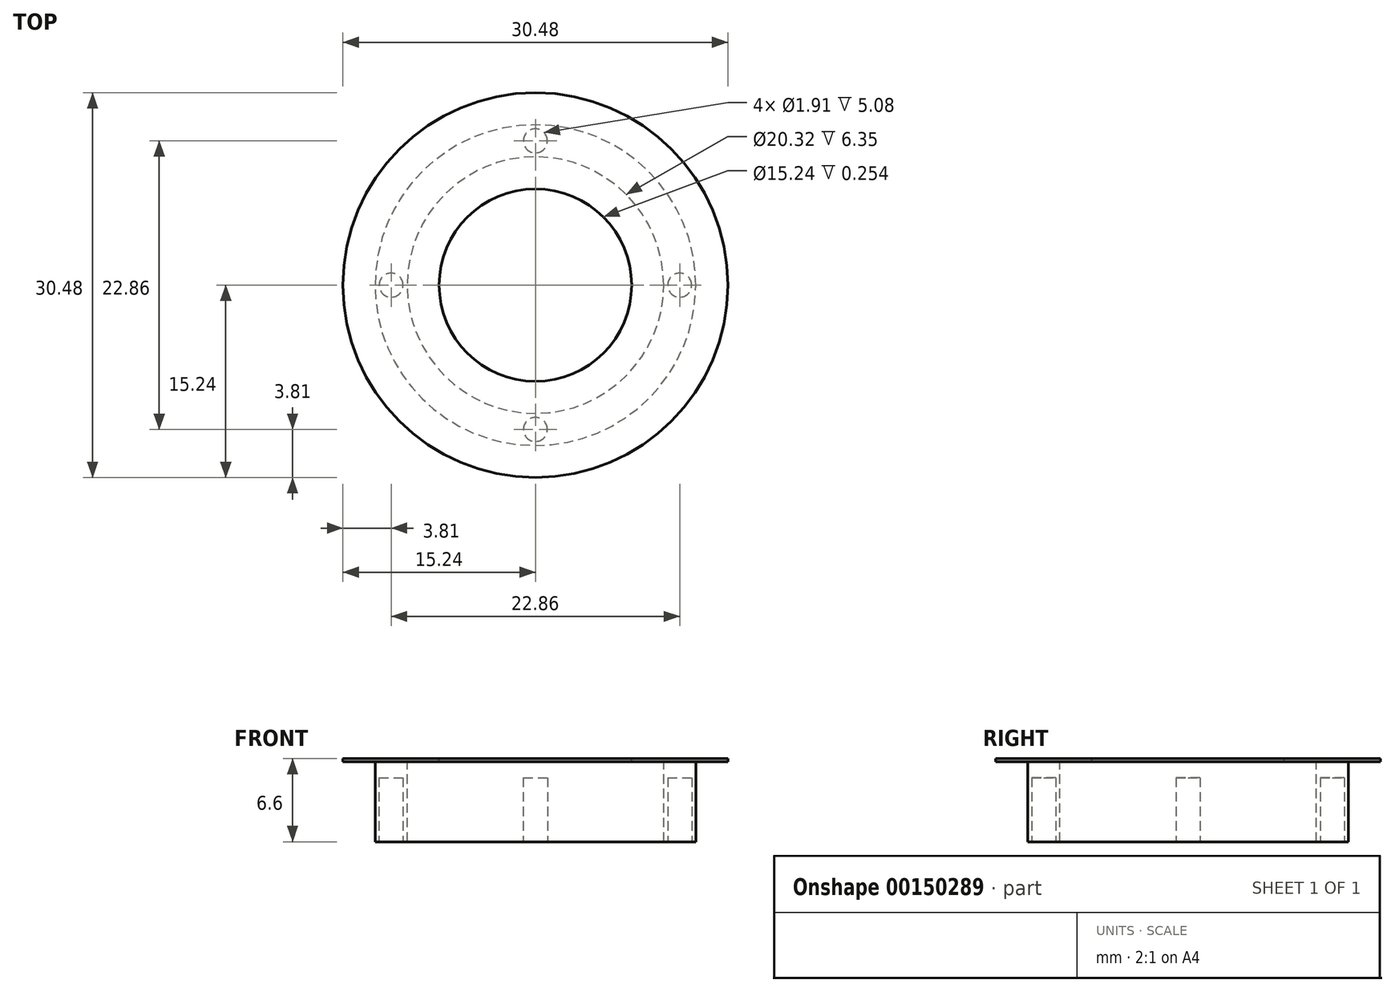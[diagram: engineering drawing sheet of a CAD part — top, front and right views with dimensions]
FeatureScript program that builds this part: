
annotation { "Feature Type Name" : "Feature", "Feature Type Description" : "" }
export const myFeature = defineFeature(function(context is Context, id is Id, definition is map)
    precondition{}
    {
        {
            var Q0;
            Q0=qCreatedBy(makeId("Front.planeOp"),FACE);
            var sketch = newSketch(context, id + "F0", { "sketchPlane" : qUnion([Q0])});
            skLineSegment(sketch, "E0.bottom", {"start": v(-12.7, 2.54) * mm, "end": v(-10.16, 2.54) * mm});
            skLineSegment(sketch, "E0.top", {"start": v(-12.7, -3.8) * mm, "end": v(-10.16, -3.8) * mm});
            skLineSegment(sketch, "E0.left", {"start": v(-12.7, 2.54) * mm, "end": v(-12.7, -3.8) * mm});
            skLineSegment(sketch, "E0.right", {"start": v(-10.16, 2.54) * mm, "end": v(-10.16, -3.8) * mm});
            skLineSegment(sketch, "E1.bottom", {"start": v(-12.7, 2.54) * mm, "end": v(-7.62, 2.54) * mm});
            skLineSegment(sketch, "E1.top", {"start": v(-12.7, 2.8) * mm, "end": v(-7.62, 2.8) * mm});
            skLineSegment(sketch, "E1.left", {"start": v(-12.7, 2.54) * mm, "end": v(-12.7, 2.8) * mm});
            skLineSegment(sketch, "E1.right", {"start": v(-7.62, 2.54) * mm, "end": v(-7.62, 2.8) * mm});
            skLineSegment(sketch, "E2", {"start": v(0, 2.9) * mm, "end": v(0, -2.8) * mm});
            skLineSegment(sketch, "E3.bottom", {"start": v(-12.7, 2.54) * mm, "end": v(-15.24, 2.54) * mm});
            skLineSegment(sketch, "E3.top", {"start": v(-12.7, 2.8) * mm, "end": v(-15.24, 2.8) * mm});
            skLineSegment(sketch, "E3.right", {"start": v(-15.24, 2.54) * mm, "end": v(-15.24, 2.8) * mm});
            skSolve(sketch);
        }
        {
            var Q0;
            Q0 = qSketchRegion(id + "F0", true);
            var Q1;
            Q1=sQuery(id+"F0.wireOp",EDGE,"E2");
            revolve(context, id + "F1", {"entities" : qUnion([Q0]), "axis" : qUnion([Q1]), "revolveType" : RevolveType.FULL});
        }
        {
            var Q0;
            Q0=makeQuery(id+"F1.opRevolve","SWEPT_FACE",FACE,{"disambiguationData":[OSD([sQuery(id+"F0.wireOp",EDGE,"E0.top")])]});
            var sketch = newSketch(context, id + "F2", { "sketchPlane" : qUnion([Q0])});
            skCircle(sketch, "E4", {"center": v(0, 11.43) * mm, "radius": 0.95 * mm});
            skCircle(sketch, "E5", {"center": v(-11.43, 0) * mm, "radius": 0.95 * mm});
            skCircle(sketch, "E6", {"center": v(11.43, 0) * mm, "radius": 0.95 * mm});
            skCircle(sketch, "E7", {"center": v(0, -11.43) * mm, "radius": 0.95 * mm});
            skSolve(sketch);
        }
        {
            var Q0;
            Q0 = qSketchRegion(id + "F2", true);
            extrude(context, id + "F3", {"entities" : qUnion([Q0]), "operationType" : NewBodyOperationType.REMOVE, "oppositeDirection" : true, "depth" : 5.08 * mm});
        }
    });
